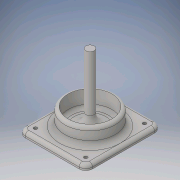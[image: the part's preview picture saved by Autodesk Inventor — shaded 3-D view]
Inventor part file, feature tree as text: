
AUTODESK INVENTOR PART (.ipt)
format: ipt  version: 2016 (Build 200138000, 138)  size: 217,088 bytes
history: native  units: in
note: dims shown in document units (in); Inventor stores cm internally (conversion verified against a paired STEP export)
features: fillet x6, sketch x4, extrude x3, hole x1
ambient origin geometry x8: Origin, YZ Plane, XZ Plane, XY Plane, X Axis, Y Axis, Z Axis, Center Point
bodies: Solid1 (feature_tree)
feature tree (14):
  extrude  "Extrusion1"  Depth=1.7717in
  extrude  "Extrusion2"  Depth=0.1969in
  fillet  "Fillet1"  Radius=1.5748in
  extrude  "Extrusion3"  Depth=0.2756in
  hole  "Hole1"  [1 undecoded]
  fillet  "Fillet2"  Radius=0.1969in
  fillet  "Fillet3"  Radius=0.1969in
  fillet  "Fillet4"  Radius=0.1969in
  fillet  "Fillet5"  Radius=0.1969in
  fillet  "Fillet6"  Radius=0.1969in
  sketch  "Sketch1"  dims[d0=0.1181in d1=0.0in d2=1.7717in]
  sketch  "Sketch2"  dims[d3=1.5748in d4=0.1969in d5=1.5748in d6=0.0in]
  sketch  "Sketch3"  dims[d7=0.2756in d8=1.0236in]
  sketch  "Sketch4"  dims[d9=1.1811in d10=0.3937in d11=0.0in d12=0.1969in d13=0.1969in d14=0.1969in d15=0.1969in d16=0.1969in d17=0.1969in d18=0.1969in d19=0.1969in d20=0.0787in d21=0.2362in d22=0.1575in d23=0.0787in d24=90.0deg d25=0.315in d26=0.8108in d27=0.1181in d28=0.0787in d29=0.1575in d30=0.0787in d31=0.0787in]
note: 1 required parameter value undecoded (feature->parameter linkage not recoverable at this tier; creation-order binding heuristic only, values carry confidence <= 0.55)
